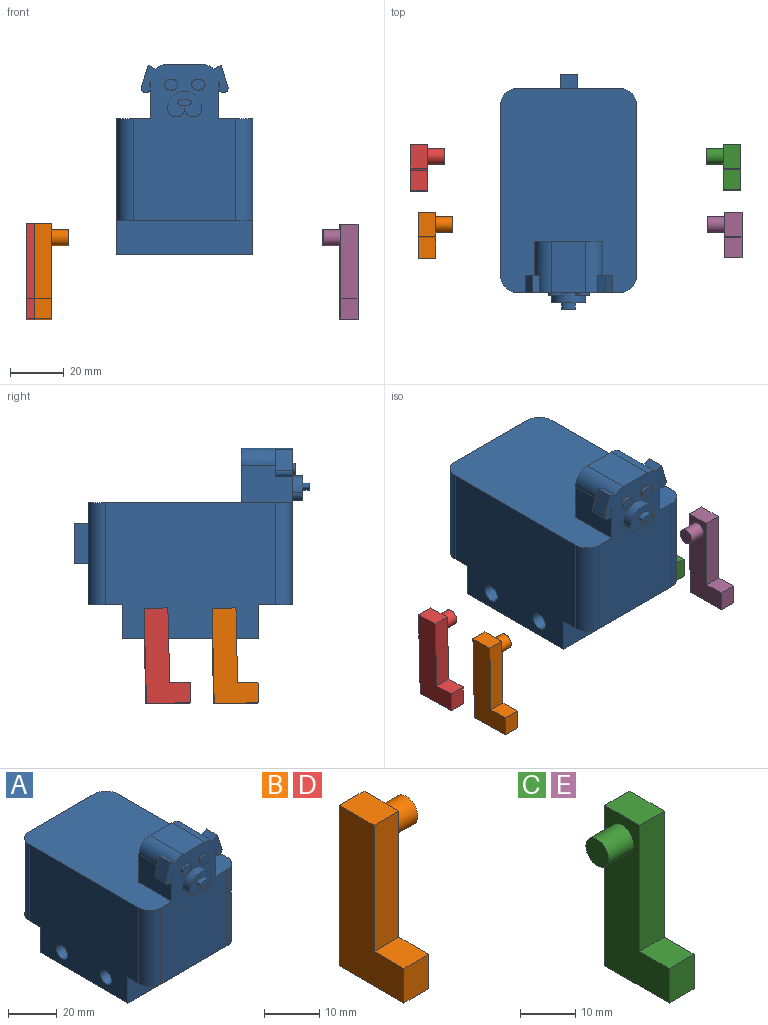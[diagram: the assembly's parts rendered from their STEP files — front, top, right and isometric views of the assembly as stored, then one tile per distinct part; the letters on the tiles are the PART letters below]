
ASSEMBLY  parts=5 mates=4
PART A: 49 faces, bbox 50.8x87.6x71.1 mm
  f0: plane 38.1x38.1mm, normal (0,1,0), area 1354.8mm2, adj f5,f6,f11,f12,f44,f45,f46,f47
  f1: plane 19.05x13.97mm, normal (1,0,0), area 261.4mm2, adj f9,f11,f18,f21,f35,f36,f37,f39
  f2: plane 19.05x13.97mm, normal (-1,0,0), area 261.4mm2, adj f9,f11,f20,f21,f28,f31,f32,f33
  f3: plane 50.8x12.7mm, normal (0,0,-1), area 627.9mm2, adj f4,f7,f8,f9,f10,f13
  f4: plane 63.5x50.8mm, normal (1,0,0), area 3001.2mm2, adj f3,f5,f10,f11,f12,f13,f14,f15
  f5: cylinder r=6.35mm len=38.1mm, axis (0,0,-1), area 380mm2, adj f0,f4,f11,f12
  f6: cylinder r=6.35mm len=38.1mm, axis (0,0,-1), area 380mm2, adj f0,f7,f11,f12
  f7: plane 63.5x50.8mm, normal (-1,0,0), area 3001.2mm2, adj f3,f6,f8,f11,f12,f13,f14,f15
  f8: cylinder r=6.35mm len=38.1mm, axis (0,0,-1), area 380mm2, adj f3,f7,f9,f11
  f9: plane 58.42x38.1mm, normal (0,-1,0), area 1877mm2, adj f1,f2,f3,f8,f10,f11,f18,f19
  f10: cylinder r=6.35mm len=38.1mm, axis (0,0,-1), area 380mm2, adj f3,f4,f9,f11
  f11: plane 76.2x50.8mm, normal (0,0,1), area 3352.5mm2, adj f0,f1,f2,f4,f5,f6,f7,f8
  f12: plane 50.8x12.7mm, normal (0,0,-1), area 627.9mm2, adj f0,f4,f5,f6,f7,f15
  f13: plane 50.8x12.7mm, normal (0,-1,0), area 645.2mm2, adj f3,f4,f7,f14
  f14: plane 50.8x50.8mm, normal (0,0,-1), area 2580.6mm2, adj f4,f7,f13,f15
  f15: plane 50.8x12.7mm, normal (0,1,0), area 645.2mm2, adj f4,f7,f12,f14
  f16: cylinder r=3.17mm len=50.8mm, axis (-1,0,0), area 1013.4mm2, adj f4,f7
  f17: cylinder r=3.17mm len=50.8mm, axis (-1,0,0), area 1013.4mm2, adj f4,f7
  f18: cylinder r=6.35mm len=19.05mm, axis (0,-1,0), area 158.3mm2, adj f1,f9,f19,f21,f34,f39
  f19: plane 19.05x12.7mm, normal (0,0,1), area 241.9mm2, adj f9,f18,f20,f21
  f20: cylinder r=6.35mm len=19.05mm, axis (0,-1,0), area 158.3mm2, adj f2,f9,f19,f21,f29,f33
  f21: plane 25.4x20.32mm, normal (0,1,0), area 498.8mm2, adj f1,f2,f11,f18,f19,f20
  f22: cylinder r=3.17mm len=6.35mm, axis (0,1,0), area 38mm2, adj f9,f23,f24,f25
  f23: cylinder r=3.17mm len=6.35mm, axis (0,1,0), area 38mm2, adj f9,f22,f24,f25
  f24: cylinder r=6.35mm len=12.7mm, axis (0,1,0), area 76mm2, adj f9,f22,f23,f25
  f25: plane 12.7x9.53mm, normal (0,-1,0), area 84.9mm2, adj f22,f23,f24,f26
  f26: extruded ~5.08x2.54mm, area 31.3mm2, adj f25,f27
  f27: plane 5.08x2.54mm, normal (0,-1,0), area 10.1mm2, adj f26
  f28: plane 6.35x1.27mm, normal (0.93,0,-0.36), area 8.6mm2, adj f2,f9,f32,f33
  f29: plane 6.35x2.77mm, normal (0.48,0,0.88), area 20mm2, adj f9,f20,f30,f33
  f30: plane 7.99x6.35mm, normal (-0.95,0,0.3), area 53.2mm2, adj f9,f29,f31,f33
  f31: cylinder r=1.78mm len=6.35mm, axis (0,-1,0), area 36.5mm2, adj f2,f9,f30,f33
  f32: cylinder r=1.78mm len=6.35mm, axis (0,-1,0), area 6.5mm2, adj f2,f9,f28,f33
  f33: plane 10.31x5.38mm, normal (0,1,0), area 27mm2, adj f2,f20,f28,f29,f30,f31,f32
  f34: plane 6.35x2.77mm, normal (-0.48,0,0.88), area 20mm2, adj f9,f18,f38,f39
  f35: plane 6.35x1.27mm, normal (-0.93,0,-0.36), area 8.6mm2, adj f1,f9,f36,f39
  f36: cylinder r=1.78mm len=6.35mm, axis (0,-1,0), area 6.5mm2, adj f1,f9,f35,f39
  f37: cylinder r=1.78mm len=6.35mm, axis (0,-1,0), area 36.5mm2, adj f1,f9,f38,f39
  f38: plane 7.99x6.35mm, normal (0.95,0,0.3), area 53.2mm2, adj f9,f34,f37,f39
  f39: plane 10.31x5.38mm, normal (0,1,0), area 27mm2, adj f1,f18,f34,f35,f36,f37,f38
  f40: extruded ~5.08x4.06mm, area 18.3mm2, adj f9,f41
  f41: plane 5.08x4.06mm, normal (0,-1,0), area 16.2mm2, adj f40
  f42: extruded ~5.08x4.06mm, area 18.3mm2, adj f9,f43
  f43: plane 5.08x4.06mm, normal (0,-1,0), area 16.2mm2, adj f42
  f44: plane 15.24x5.08mm, normal (1,0,0), area 77.4mm2, adj f0,f45,f47,f48
  f45: plane 6.35x5.08mm, normal (0,0,-1), area 32.3mm2, adj f0,f44,f46,f48
  f46: plane 15.24x5.08mm, normal (-1,0,0), area 77.4mm2, adj f0,f45,f47,f48
  f47: plane 6.35x5.08mm, normal (0,0,1), area 32.3mm2, adj f0,f44,f46,f48
  f48: plane 15.24x6.35mm, normal (0,1,0), area 96.8mm2, adj f44,f45,f46,f47
PART B: 10 faces, bbox 12.7x16.5x35.6 mm
  f0: plane 7.62x6.35mm, normal (0,-1,0), area 48.4mm2, adj f1,f5,f6,f7
  f1: plane 16.51x6.35mm, normal (0,0,-1), area 104.8mm2, adj f0,f2,f6,f7
  f2: plane 35.56x6.35mm, normal (0,1,0), area 225.8mm2, adj f1,f3,f6,f7
  f3: plane 8.89x6.35mm, normal (0,0,1), area 56.5mm2, adj f2,f4,f6,f7
  f4: plane 27.94x6.35mm, normal (0,-1,0), area 177.4mm2, adj f3,f5,f6,f7
  f5: plane 7.62x6.35mm, normal (0,0,1), area 48.4mm2, adj f0,f4,f6,f7
  f6: plane 35.56x16.51mm, normal (1,0,0), area 347.4mm2, adj f0,f1,f2,f3,f4,f5,f8
  f7: plane 35.56x16.51mm, normal (-1,0,0), area 374.2mm2, adj f0,f1,f2,f3,f4,f5
  f8: cylinder r=2.92mm len=6.35mm, axis (-1,0,0), area 116.5mm2, adj f6,f9
  f9: plane 5.84x5.84mm, normal (1,0,0), area 26.8mm2, adj f8
PART C: 10 faces, bbox 12.7x16.5x35.6 mm
  f0: plane 7.62x6.35mm, normal (0,-1,0), area 48.4mm2, adj f1,f5,f6,f7
  f1: plane 16.51x6.35mm, normal (0,0,-1), area 104.8mm2, adj f0,f2,f6,f7
  f2: plane 35.56x6.35mm, normal (0,1,0), area 225.8mm2, adj f1,f3,f6,f7
  f3: plane 8.89x6.35mm, normal (0,0,1), area 56.5mm2, adj f2,f4,f6,f7
  f4: plane 27.94x6.35mm, normal (0,-1,0), area 177.4mm2, adj f3,f5,f6,f7
  f5: plane 7.62x6.35mm, normal (0,0,1), area 48.4mm2, adj f0,f4,f6,f7
  f6: plane 35.56x16.51mm, normal (1,0,0), area 374.2mm2, adj f0,f1,f2,f3,f4,f5
  f7: plane 35.56x16.51mm, normal (-1,0,0), area 347.4mm2, adj f0,f1,f2,f3,f4,f5,f8
  f8: cylinder r=2.92mm len=6.35mm, axis (1,0,0), area 116.5mm2, adj f7,f9
  f9: plane 5.84x5.84mm, normal (-1,0,0), area 26.8mm2, adj f8
PART D: same geometry as B
PART E: same geometry as C
PLACE A t=(-18.83,13.98,1.62)mm fixed
PLACE B rot(axis=(-1,0,0),1.3deg) t=(-49.32,43.15,-35.3)mm
PLACE C rot(axis=(-1,0,0),0.8deg) t=(64.2,68.81,-35.27)mm
PLACE D rot(axis=(-1,0,0),1.5deg) t=(-52.64,68.43,-35.32)mm
PLACE E rot(axis=(-1,0,0),0.6deg) t=(64.92,43.49,-35.26)mm
MATE cylindrical A.f17 <-> C.f8  axis (1,0,0) through (31.97,64.78,-4.73)mm
MATE cylindrical D.f8 <-> A.f17  axis (1,0,0) through (-46.29,64.78,-4.73)mm
MATE cylindrical B.f8 <-> A.f16  axis (-1,0,0) through (-42.97,39.38,-4.73)mm
MATE cylindrical A.f16 <-> E.f8  axis (1,0,0) through (31.97,39.38,-4.73)mm
